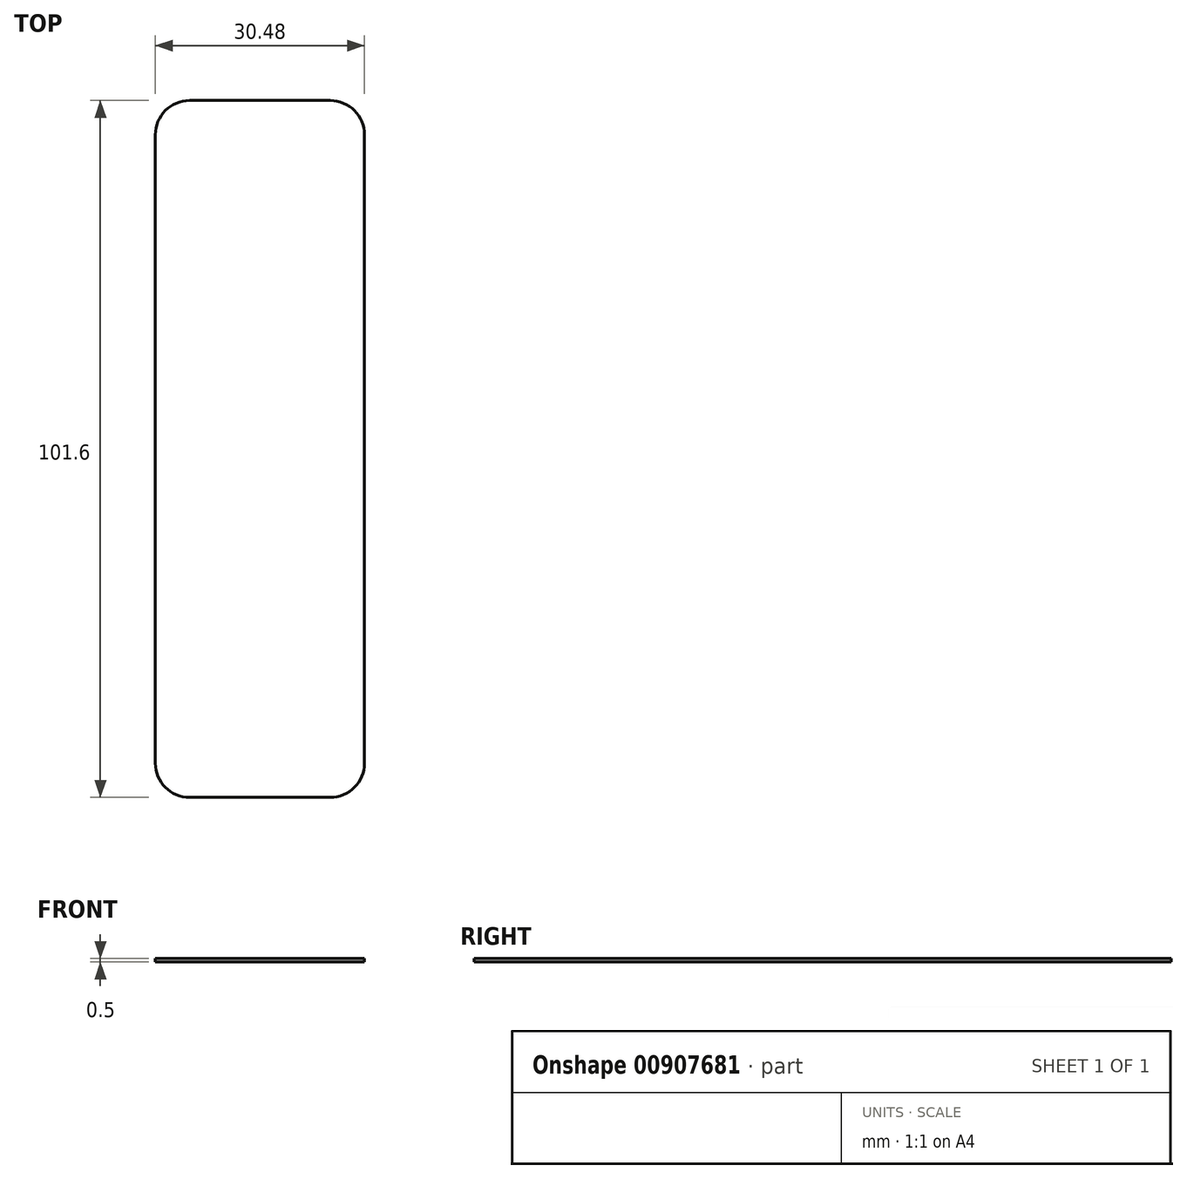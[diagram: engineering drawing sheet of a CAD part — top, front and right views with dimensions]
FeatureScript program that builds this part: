
annotation { "Feature Type Name" : "Feature", "Feature Type Description" : "" }
export const myFeature = defineFeature(function(context is Context, id is Id, definition is map)
    precondition{}
    {
        {
            var Q0;
            Q0=qCreatedBy(makeId("Top.planeOp"),FACE);
            var sketch = newSketch(context, id + "F0", { "sketchPlane" : qUnion([Q0])});
            skLineSegment(sketch, "E0.bottom", {"start": v(15.24, -50.8) * mm, "end": v(-15.24, -50.8) * mm});
            skLineSegment(sketch, "E0.top", {"start": v(15.24, 50.8) * mm, "end": v(-15.24, 50.8) * mm});
            skLineSegment(sketch, "E0.left", {"start": v(15.24, -50.8) * mm, "end": v(15.24, 50.8) * mm});
            skLineSegment(sketch, "E0.right", {"start": v(-15.24, -50.8) * mm, "end": v(-15.24, 50.8) * mm});
            skPoint(sketch, "E0.middle", {"position": v(0, 0) * mm});
            skSolve(sketch);
        }
        {
            var Q0;
            Q0=makeQuery(id+"F0.imprint","IMPRINT",FACE,{"disambiguationData":[TD([[makeQuery(id+"F0.imprint","IMPRINT",EDGE,{"derivedFrom":sQuery(id+"F0.wireOp",EDGE,"E0.bottom")}),-1.0]])]});
            extrude(context, id + "F1", {"entities" : qUnion([Q0]), "depth" : .5 * mm, "offsetDistance" : 25 * mm});
        }
        {
            var Q0;
            Q0=makeQuery(id+"F1.opExtrude","SWEPT_EDGE",EDGE,{"disambiguationData":[OSD([sQuery(id+"F0.wireOp",EDGE,"E0.bottom"),sQuery(id+"F0.wireOp",EDGE,"E0.left")])]});
            var Q1;
            Q1=makeQuery(id+"F1.opExtrude","SWEPT_EDGE",EDGE,{"disambiguationData":[OSD([sQuery(id+"F0.wireOp",EDGE,"E0.bottom"),sQuery(id+"F0.wireOp",EDGE,"E0.right")])]});
            var Q2;
            Q2=makeQuery(id+"F1.opExtrude","SWEPT_EDGE",EDGE,{"disambiguationData":[OSD([sQuery(id+"F0.wireOp",EDGE,"E0.top"),sQuery(id+"F0.wireOp",EDGE,"E0.right")])]});
            var Q3;
            Q3=makeQuery(id+"F1.opExtrude","SWEPT_EDGE",EDGE,{"disambiguationData":[OSD([sQuery(id+"F0.wireOp",EDGE,"E0.top"),sQuery(id+"F0.wireOp",EDGE,"E0.left")])]});
            fillet(context, id + "F2", {"entities" : qUnion([Q0, Q1, Q2, Q3]), "radius" : 5 * mm, "tangentPropagation" : true, "allowEdgeOverflow" : false});
        }
        {
            var Q0;
            Q0=makeQuery(id+"F1.opExtrude","CAP_FACE",FACE,{"disambiguationData":[OSD([sQuery(id+"F0.wireOp",EDGE,"E0.bottom"),sQuery(id+"F0.wireOp",EDGE,"E0.top"),sQuery(id+"F0.wireOp",EDGE,"E0.left"),sQuery(id+"F0.wireOp",EDGE,"E0.right")])],"isStart":false});
            cPlane(context, id + "F3", {"entities" : qUnion([Q0]), "cplaneType" : CPlaneType.OFFSET, "offset" : 25 * mm, "width" : 150 * mm, "height" : 150 * mm});
        }
        {
            var Q0;
            Q0=qCreatedBy(id+"F3.planeOp",FACE);
            var sketch = newSketch(context, id + "F4", { "sketchPlane" : qUnion([Q0])});
            skCircle(sketch, "E1", {"center": v(0, 0) * mm, "radius": 12.6 * mm});
            skSolve(sketch);
        }
        {
            var Q0;
            Q0=makeQuery(id+"F4.imprint","IMPRINT",FACE,{"disambiguationData":[TD([[makeQuery(id+"F4.imprint","IMPRINT",EDGE,{"derivedFrom":sQuery(id+"F4.wireOp",EDGE,"E1")}),1.0]])]});
            extrude(context, id + "F5", {"entities" : qUnion([Q0]), "depth" : .5 * mm, "offsetDistance" : 25 * mm});
        }
        {
            var Q0;
            Q0=makeQuery(id+"F5.opExtrude","SWEPT_BODY",BODY,{"disambiguationData":[OSD([sQuery(id+"F4.wireOp",EDGE,"E1")])]});
            deleteBodies(context, id + "F6", {"entities" : qUnion([Q0])});
        }
    });
